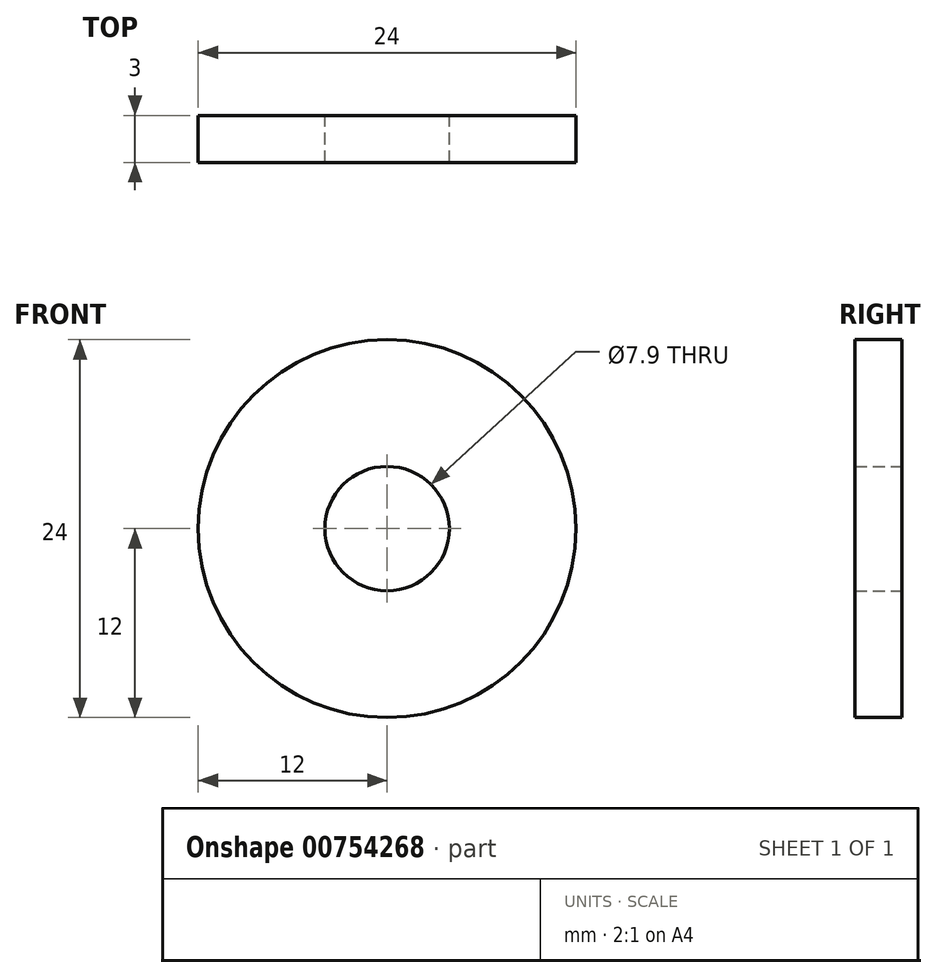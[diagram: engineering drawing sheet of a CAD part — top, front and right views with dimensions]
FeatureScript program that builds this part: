
annotation { "Feature Type Name" : "Feature", "Feature Type Description" : "" }
export const myFeature = defineFeature(function(context is Context, id is Id, definition is map)
    precondition{}
    {
        {
            var Q0;
            Q0=qCreatedBy(makeId("Front.planeOp"),FACE);
            var sketch = newSketch(context, id + "F0", { "sketchPlane" : qUnion([Q0])});
            skCircle(sketch, "E0", {"center": v(0, 0) * mm, "radius": 12 * mm});
            skCircle(sketch, "E1", {"center": v(0, 0) * mm, "radius": 3.95 * mm});
            skSolve(sketch);
        }
        {
            var Q0;
            Q0=makeQuery(id+"F0.imprint","IMPRINT",FACE,{"disambiguationData":[TD([[makeQuery(id+"F0.imprint","IMPRINT",EDGE,{"derivedFrom":sQuery(id+"F0.wireOp",EDGE,"E0")}),1.0]])]});
            extrude(context, id + "F1", {"entities" : qUnion([Q0]), "depth" : 3 * mm, "offsetDistance" : 25 * mm});
        }
    });
